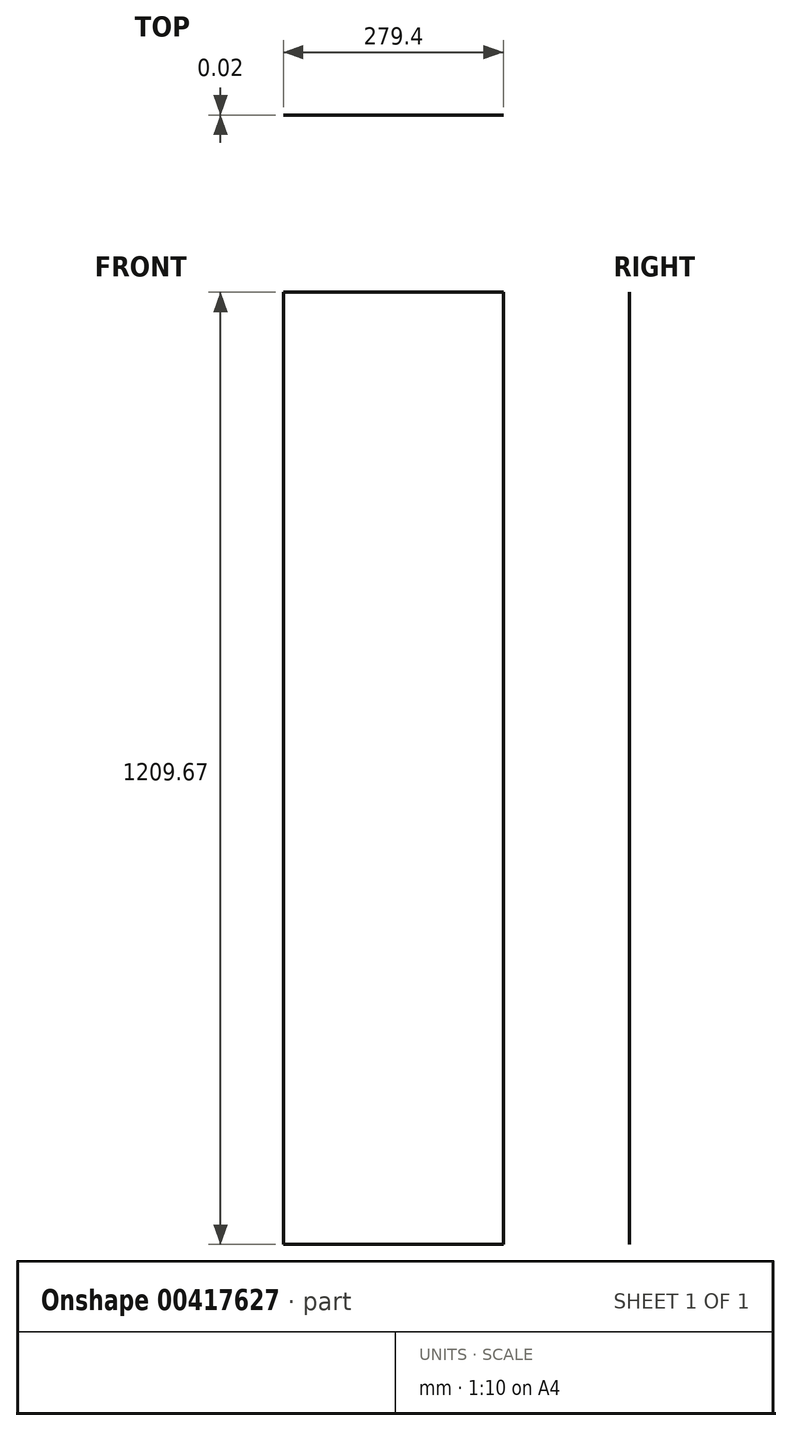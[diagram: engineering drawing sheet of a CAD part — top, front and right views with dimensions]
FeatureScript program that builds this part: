
annotation { "Feature Type Name" : "Feature", "Feature Type Description" : "" }
export const myFeature = defineFeature(function(context is Context, id is Id, definition is map)
    precondition{}
    {
        {
            var Q0;
            Q0=qCreatedBy(makeId("Front.planeOp"),FACE);
            var sketch = newSketch(context, id + "F0", { "sketchPlane" : qUnion([Q0])});
            skLineSegment(sketch, "E0.bottom", {"start": v(0, 0) * mm, "end": v(279.4, 0) * mm});
            skLineSegment(sketch, "E0.top", {"start": v(0, 1209.67) * mm, "end": v(279.4, 1209.67) * mm});
            skLineSegment(sketch, "E0.left", {"start": v(0, 0) * mm, "end": v(0, 1209.67) * mm});
            skLineSegment(sketch, "E0.right", {"start": v(279.4, 0) * mm, "end": v(279.4, 1209.67) * mm});
            skSolve(sketch);
        }
        {
            var Q0;
            Q0=makeQuery(id+"F0.imprint","IMPRINT",FACE,{"disambiguationData":[TD([[makeQuery(id+"F0.imprint","IMPRINT",EDGE,{"derivedFrom":sQuery(id+"F0.wireOp",EDGE,"E0.bottom")}),1.0]])]});
            extrude(context, id + "F1", {"entities" : qUnion([Q0]), "depth" : 5 / 203.2 * mm});
        }
    });
